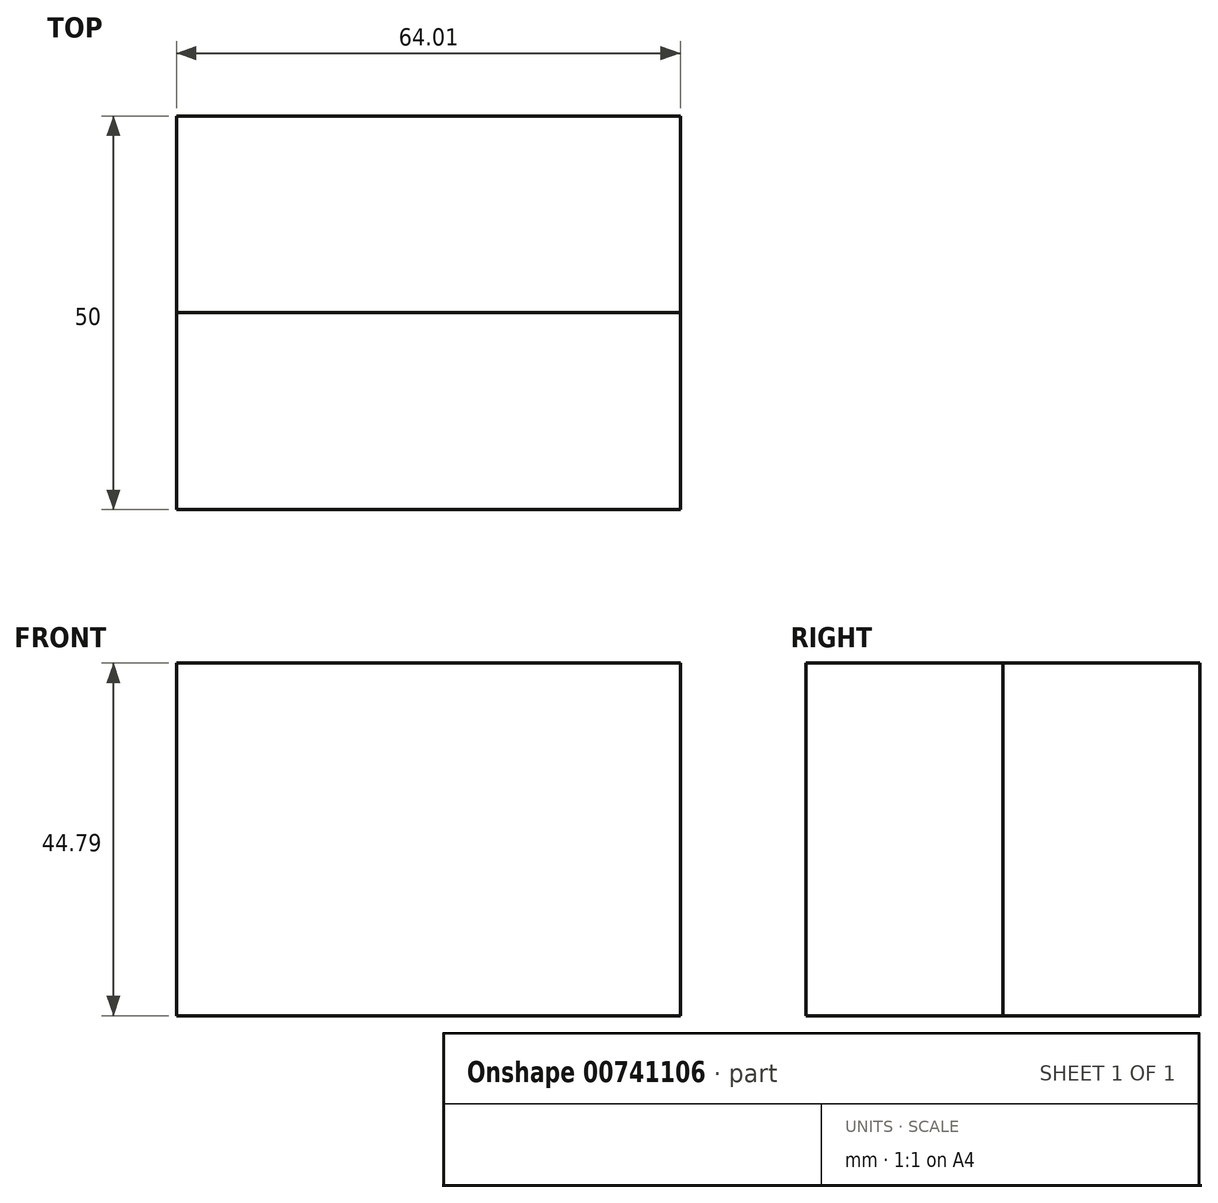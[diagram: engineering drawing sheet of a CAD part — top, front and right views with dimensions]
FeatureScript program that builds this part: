
annotation { "Feature Type Name" : "Feature", "Feature Type Description" : "" }
export const myFeature = defineFeature(function(context is Context, id is Id, definition is map)
    precondition{}
    {
        {
            var Q0;
            Q0=qCreatedBy(makeId("Front.planeOp"),FACE);
            var sketch = newSketch(context, id + "F0", { "sketchPlane" : qUnion([Q0])});
            skLineSegment(sketch, "E0.bottom", {"start": v(-70.45, 41.15) * mm, "end": v(-6.44, 41.15) * mm});
            skLineSegment(sketch, "E0.top", {"start": v(-70.45, -3.64) * mm, "end": v(-6.44, -3.64) * mm});
            skLineSegment(sketch, "E0.left", {"start": v(-70.45, 41.15) * mm, "end": v(-70.45, -3.64) * mm});
            skLineSegment(sketch, "E0.right", {"start": v(-6.44, 41.15) * mm, "end": v(-6.44, -3.64) * mm});
            skSolve(sketch);
        }
        {
            var Q0;
            Q0 = qSketchRegion(id + "F0", true);
            extrude(context, id + "F1", {"entities" : qUnion([Q0]), "depth" : 25 * mm, "offsetDistance" : 25 * mm});
        }
        {
            var Q0;
            Q0=makeQuery(id+"F1.opExtrude","CAP_FACE",FACE,{"disambiguationData":[OSD([sQuery(id+"F0.wireOp",EDGE,"E0.bottom"),sQuery(id+"F0.wireOp",EDGE,"E0.top"),sQuery(id+"F0.wireOp",EDGE,"E0.left"),sQuery(id+"F0.wireOp",EDGE,"E0.right")])],"isStart":true});
            extrude(context, id + "F2", {"entities" : qUnion([Q0]), "depth" : 25 * mm, "offsetDistance" : 25 * mm});
        }
    });
